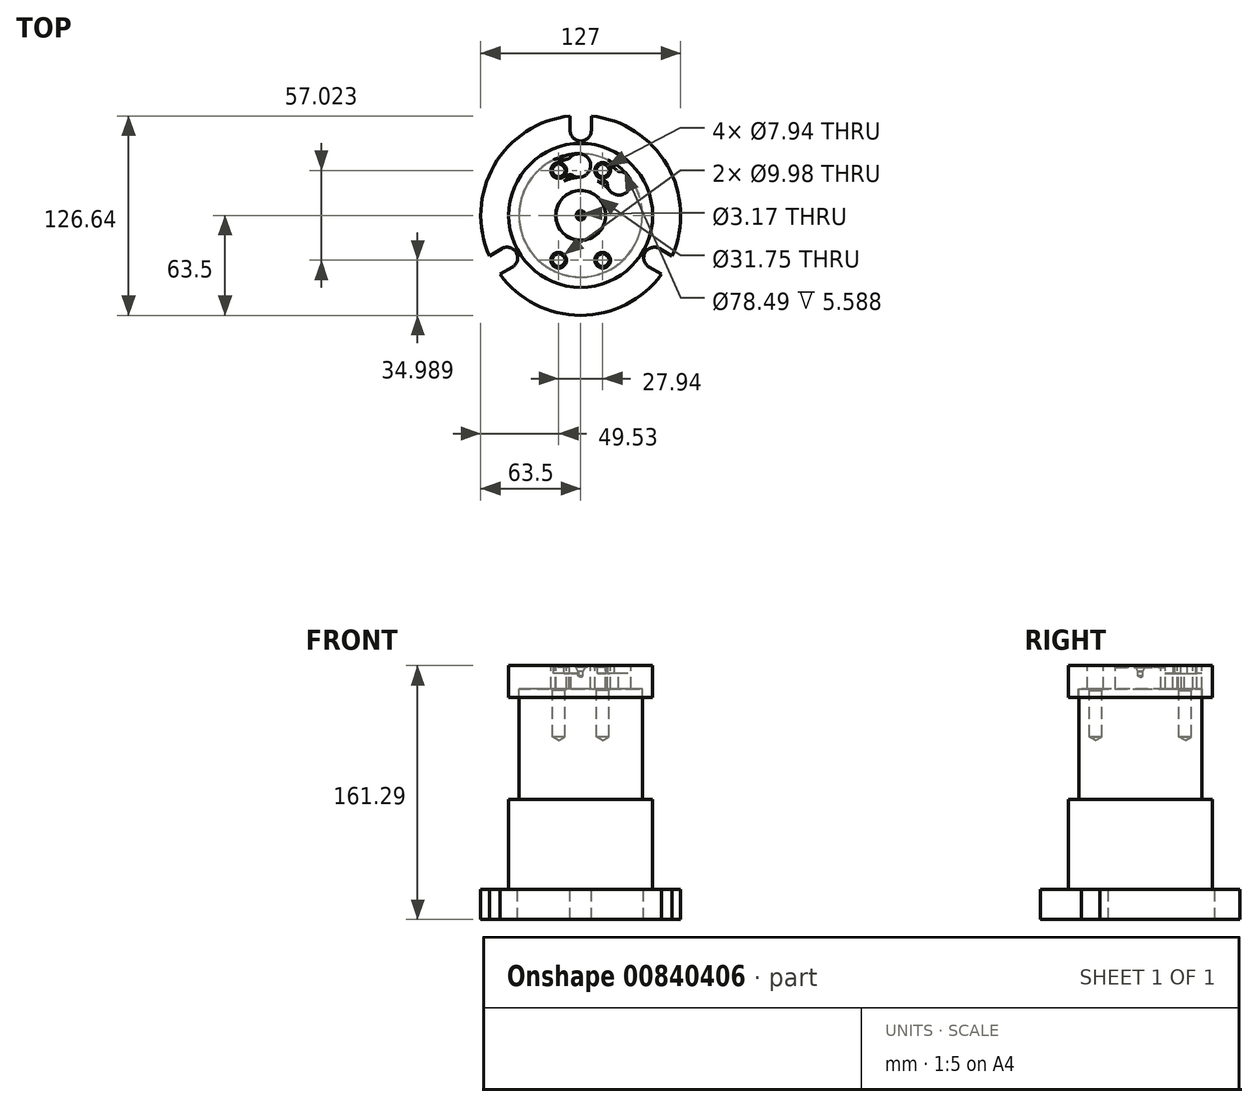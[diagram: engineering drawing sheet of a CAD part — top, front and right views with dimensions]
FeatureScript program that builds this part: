
annotation { "Feature Type Name" : "Feature", "Feature Type Description" : "" }
export const myFeature = defineFeature(function(context is Context, id is Id, definition is map)
    precondition{}
    {
        {
            var Q0;
            Q0=qCreatedBy(makeId("Front.planeOp"),FACE);
            var sketch = newSketch(context, id + "F0", { "sketchPlane" : qUnion([Q0])});
            skLineSegment(sketch, "E0", {"start": v(0, 0) * mm, "end": v(0, -38.57) * mm, "construction": true});
            skLineSegment(sketch, "E1", {"start": v(-15.88, 0) * mm, "end": v(-15.88, -14.73) * mm});
            skLineSegment(sketch, "E2", {"start": v(-15.88, -14.73) * mm, "end": v(-39.24, -14.73) * mm});
            skLineSegment(sketch, "E3", {"start": v(-39.24, -14.73) * mm, "end": v(-39.24, -20.32) * mm});
            skLineSegment(sketch, "E4", {"start": v(-39.24, -20.32) * mm, "end": v(-45.72, -20.32) * mm});
            skLineSegment(sketch, "E5", {"start": v(-45.72, -20.32) * mm, "end": v(-45.72, 0) * mm});
            skLineSegment(sketch, "E6", {"start": v(-45.72, 0) * mm, "end": v(-15.88, 0) * mm});
            skSolve(sketch);
        }
        {
            var Q0;
            Q0 = qSketchRegion(id + "F0", true);
            var Q1;
            Q1=sQuery(id+"F0.wireOp",EDGE,"E0");
            revolve(context, id + "F1", {"surfaceOperationType" : NewSurfaceOperationType.NEW, "entities" : qUnion([Q0]), "axis" : qUnion([Q1]), "revolveType" : RevolveType.FULL});
        }
        {
            var Q0;
            Q0=makeQuery(id+"F1.opRevolve","SWEPT_FACE",FACE,{"disambiguationData":[OSD([sQuery(id+"F0.wireOp",EDGE,"E6")])]});
            var sketch = newSketch(context, id + "F2", { "sketchPlane" : qUnion([Q0])});
            skCircle(sketch, "E7", {"center": v(0, 0) * mm, "radius": 31.75 * mm, "construction": true});
            skCircle(sketch, "E8", {"center": v(-13.97, 28.51) * mm, "radius": 5 * mm});
            skCircle(sketch, "E9", {"center": v(13.97, 28.51) * mm, "radius": 5 * mm});
            skCircle(sketch, "E10", {"center": v(13.97, -28.51) * mm, "radius": 5 * mm});
            skCircle(sketch, "E11", {"center": v(-13.97, -28.51) * mm, "radius": 5 * mm});
            skLineSegment(sketch, "E12", {"start": v(-13.97, 28.51) * mm, "end": v(13.97, 28.51) * mm, "construction": true});
            skLineSegment(sketch, "E13", {"start": v(-13.97, -28.51) * mm, "end": v(13.97, -28.51) * mm, "construction": true});
            skSolve(sketch);
        }
        {
            var Q0;
            Q0 = qSketchRegion(id + "F2", true);
            extrude(context, id + "F3", {"entities" : qUnion([Q0]), "operationType" : NewBodyOperationType.REMOVE, "endBound" : BoundingType.THROUGH_ALL, "oppositeDirection" : true, "depth" : 25.4 * mm, "offsetDistance" : 25.4 * mm});
        }
        {
            var Q0;
            Q0=makeQuery(id+"F1.opRevolve","SWEPT_FACE",FACE,{"disambiguationData":[OSD([sQuery(id+"F0.wireOp",EDGE,"E6")])]});
            var sketch = newSketch(context, id + "F4", { "sketchPlane" : qUnion([Q0])});
            skCircle(sketch, "E14", {"center": v(0, 0) * mm, "radius": 31.75 * mm, "construction": true});
            skPoint(sketch, "E15", {"position": v(-13.97, 28.51) * mm});
            skArc(sketch, "E16", {"start": v(-6.07, 26.06) * mm, "mid": v(6.27, 32.66) * mm, "end": v(-7.32, 36) * mm});
            skLineSegment(sketch, "E17", {"start": v(0, 0) * mm, "end": v(-1.17, 31.73) * mm, "construction": true});
            skLineSegment(sketch, "E18", {"start": v(0, 0) * mm, "end": v(-13.97, 28.51) * mm, "construction": true});
            skArc(sketch, "E19", {"start": v(16.88, 20.77) * mm, "mid": v(29.65, 15.06) * mm, "end": v(23.97, 27.85) * mm});
            skPoint(sketch, "E20", {"position": v(13.97, 28.51) * mm});
            skLineSegment(sketch, "E21", {"start": v(0, 0) * mm, "end": v(13.97, 28.51) * mm, "construction": true});
            skLineSegment(sketch, "E22", {"start": v(0, 0) * mm, "end": v(24.36, 20.36) * mm, "construction": true});
            skArc(sketch, "E23.0", {"start": v(16.17, 33) * mm, "mid": v(9.49, 30.7) * mm, "end": v(11.77, 24.03) * mm});
            skArc(sketch, "E23.1", {"start": v(-16.17, 33) * mm, "mid": v(-18.45, 26.32) * mm, "end": v(-11.77, 24.03) * mm});
            skArc(sketch, "E24", {"start": v(23.97, 27.85) * mm, "mid": v(20.23, 30.67) * mm, "end": v(16.17, 33) * mm});
            skArc(sketch, "E25.trimOffspring", {"start": v(-6.07, 26.06) * mm, "mid": v(-8.98, 25.2) * mm, "end": v(-11.77, 24.03) * mm});
            skArc(sketch, "E26.trimOffspring", {"start": v(-7.32, 36) * mm, "mid": v(-11.84, 34.78) * mm, "end": v(-16.17, 33) * mm});
            skArc(sketch, "E27.trimOffspring", {"start": v(16.88, 20.77) * mm, "mid": v(14.42, 22.54) * mm, "end": v(11.77, 24.03) * mm});
            skSolve(sketch);
        }
        {
            var Q0;
            Q0 = qSketchRegion(id + "F4", true);
            extrude(context, id + "F5", {"entities" : qUnion([Q0]), "operationType" : NewBodyOperationType.REMOVE, "endBound" : BoundingType.THROUGH_ALL, "oppositeDirection" : true, "depth" : 25.4 * mm, "offsetDistance" : 25.4 * mm});
        }
        {
            var Q0;
            Q0=makeQuery(id+"F1.opRevolve","SWEPT_FACE",FACE,{"disambiguationData":[OSD([sQuery(id+"F0.wireOp",EDGE,"E6")])]});
            var sketch = newSketch(context, id + "F6", { "sketchPlane" : qUnion([Q0])});
            skCircle(sketch, "E28", {"center": v(-13.97, 28.51) * mm, "radius": 7.5 * mm});
            skCircle(sketch, "E29", {"center": v(13.97, 28.51) * mm, "radius": 7.5 * mm});
            skCircle(sketch, "E30", {"center": v(0, 0) * mm, "radius": 24.26 * mm});
            skCircle(sketch, "E31", {"center": v(0, 0) * mm, "radius": 39.24 * mm});
            skSolve(sketch);
        }
        {
            var Q0;
            {var subQ0=makeQuery(id+"F5.boolean.opBoolean","COPY",EDGE,{"derivedFrom":makeQuery(id+"F5.opExtrude","CAP_EDGE",EDGE,{"disambiguationData":[OSD([sQuery(id+"F4.wireOp",EDGE,"E25.trimOffspring")])],"isStart":true})});Q0=makeQuery(id+"F6.imprint","IMPRINT",FACE,{"disambiguationData":[TD([[makeQuery(id+"F6.imprint","IMPRINT",EDGE,{"derivedFrom":subQ0}),1.0]])]});}
            var Q1;
            {var subQ0=sQuery(id+"F6.wireOp",EDGE,"E30");var subQ1=sQuery(id+"F6.wireOp",EDGE,"E28");var subQ2=makeQuery(id+"F6.imprint","INTERSECT",VERTEX,{"derivedFrom":[subQ1,subQ0]});Q1=makeQuery(id+"F6.imprint","IMPRINT",FACE,{"disambiguationData":[TD([[makeQuery(id+"F6.imprint","IMPRINT",EDGE,{"disambiguationData":[TD([[subQ2,-1.0]])],"derivedFrom":subQ1}),-1.0]])]});}
            var Q2;
            {var subQ0=sQuery(id+"F6.wireOp",EDGE,"E31");var subQ1=sQuery(id+"F6.wireOp",EDGE,"E28");var subQ2=makeQuery(id+"F6.imprint","INTERSECT",VERTEX,{"derivedFrom":[subQ1,subQ0]});Q2=makeQuery(id+"F6.imprint","IMPRINT",FACE,{"disambiguationData":[TD([[makeQuery(id+"F6.imprint","IMPRINT",EDGE,{"disambiguationData":[TD([[subQ2,1.0]])],"derivedFrom":subQ1}),-1.0]])]});}
            var Q3;
            {var subQ10=makeQuery(id+"F5.boolean.opBoolean","COPY",EDGE,{"derivedFrom":makeQuery(id+"F5.opExtrude","CAP_EDGE",EDGE,{"disambiguationData":[OSD([sQuery(id+"F4.wireOp",EDGE,"E24")])],"isStart":true})});Q3=makeQuery(id+"F6.imprint","IMPRINT",FACE,{"disambiguationData":[TD([[makeQuery(id+"F6.imprint","IMPRINT",EDGE,{"derivedFrom":subQ10}),-1.0]])]});}
            var Q4;
            {var subQ0=sQuery(id+"F6.wireOp",EDGE,"E31");var subQ1=sQuery(id+"F6.wireOp",EDGE,"E29");var subQ2=makeQuery(id+"F6.imprint","INTERSECT",VERTEX,{"derivedFrom":[subQ1,subQ0]});Q4=makeQuery(id+"F6.imprint","IMPRINT",FACE,{"disambiguationData":[TD([[makeQuery(id+"F6.imprint","IMPRINT",EDGE,{"disambiguationData":[TD([[subQ2,1.0]])],"derivedFrom":subQ1}),-1.0]])]});}
            var Q5;
            {var subQ0=sQuery(id+"F6.wireOp",EDGE,"E30");var subQ1=sQuery(id+"F6.wireOp",EDGE,"E29");var subQ2=makeQuery(id+"F6.imprint","INTERSECT",VERTEX,{"derivedFrom":[subQ1,subQ0]});Q5=makeQuery(id+"F6.imprint","IMPRINT",FACE,{"disambiguationData":[TD([[makeQuery(id+"F6.imprint","IMPRINT",EDGE,{"disambiguationData":[TD([[subQ2,-1.0]])],"derivedFrom":subQ1}),-1.0]])]});}
            var Q6;
            {var subQ0=makeQuery(id+"F3.boolean.opBoolean","COPY",EDGE,{"derivedFrom":makeQuery(id+"F3.opExtrude","CAP_EDGE",EDGE,{"disambiguationData":[OSD([sQuery(id+"F2.wireOp",EDGE,"E8")])],"isStart":true})});Q6=makeQuery(id+"F6.imprint","IMPRINT",FACE,{"disambiguationData":[TD([[makeQuery(id+"F6.imprint","IMPRINT",EDGE,{"derivedFrom":subQ0}),-1.0]])]});}
            var Q7;
            {var subQ4=makeQuery(id+"F3.boolean.opBoolean","COPY",EDGE,{"derivedFrom":makeQuery(id+"F3.opExtrude","CAP_EDGE",EDGE,{"disambiguationData":[OSD([sQuery(id+"F2.wireOp",EDGE,"E9")])],"isStart":true})});Q7=makeQuery(id+"F6.imprint","IMPRINT",FACE,{"disambiguationData":[TD([[makeQuery(id+"F6.imprint","IMPRINT",EDGE,{"derivedFrom":subQ4}),-1.0]])]});}
            extrude(context, id + "F7", {"entities" : qUnion([Q0, Q1, Q2, Q3, Q4, Q5, Q6, Q7]), "operationType" : NewBodyOperationType.REMOVE, "oppositeDirection" : true, "depth" : 5.08 * mm, "offsetDistance" : 25.4 * mm});
        }
        {
            var Q0;
            Q0=qCreatedBy(makeId("Right.planeOp"),FACE);
            var sketch = newSketch(context, id + "F8", { "sketchPlane" : qUnion([Q0])});
            skLineSegment(sketch, "E32", {"start": v(-39.12, -85.1) * mm, "end": v(-39.12, -14.73) * mm});
            skLineSegment(sketch, "E33", {"start": v(-39.12, -14.73) * mm, "end": v(-15.75, -14.73) * mm});
            skLineSegment(sketch, "E34", {"start": v(-15.75, -14.73) * mm, "end": v(-15.75, -1.27) * mm});
            skLineSegment(sketch, "E35", {"start": v(-15.75, -1.27) * mm, "end": v(0, -1.27) * mm});
            skLineSegment(sketch, "E36", {"start": v(0, -1.27) * mm, "end": v(0, -161.3) * mm});
            skLineSegment(sketch, "E37", {"start": v(0, -161.3) * mm, "end": v(-63.5, -161.3) * mm});
            skLineSegment(sketch, "E38", {"start": v(-63.5, -161.3) * mm, "end": v(-63.5, -142.24) * mm});
            skLineSegment(sketch, "E39", {"start": v(-63.5, -142.24) * mm, "end": v(-45.72, -142.24) * mm});
            skLineSegment(sketch, "E40", {"start": v(-45.72, -142.24) * mm, "end": v(-45.72, -85.1) * mm});
            skLineSegment(sketch, "E41", {"start": v(-45.72, -85.1) * mm, "end": v(-39.12, -85.1) * mm});
            skLineSegment(sketch, "E42", {"start": v(0, 32.69) * mm, "end": v(0, -171.35) * mm, "construction": true});
            skSolve(sketch);
        }
        {
            var Q0;
            Q0 = qSketchRegion(id + "F8", true);
            var Q1;
            Q1=sQuery(id+"F8.wireOp",EDGE,"E42");
            revolve(context, id + "F9", {"surfaceOperationType" : NewSurfaceOperationType.NEW, "entities" : qUnion([Q0]), "axis" : qUnion([Q1]), "revolveType" : RevolveType.FULL});
        }
        {
            var Q0;
            Q0=makeQuery(id+"F9.opRevolve","SWEPT_FACE",FACE,{"disambiguationData":[OSD([sQuery(id+"F8.wireOp",EDGE,"E33")])]});
            var sketch = newSketch(context, id + "F10", { "sketchPlane" : qUnion([Q0])});
            skSolve(sketch);
        }
        {
            var Q0;
            {var subQ0=sQuery(id+"F8.wireOp",EDGE,"E33");Q0=makeQuery(id+"F10.imprint","IMPRINT",FACE,{"disambiguationData":[TD([[makeQuery(id+"F10.imprint","IMPRINT",EDGE,{"derivedFrom":makeQuery(id+"F9.opRevolve","SWEPT_EDGE",EDGE,{"disambiguationData":[OSD([sQuery(id+"F8.wireOp",EDGE,"E32"),subQ0])]})}),1.0]])]});}
            var sketch = newSketch(context, id + "F11", { "sketchPlane" : qUnion([Q0])});
            skPoint(sketch, "E43", {"position": v(-13.97, 28.51) * mm});
            skPoint(sketch, "E44", {"position": v(13.97, 28.51) * mm});
            skPoint(sketch, "E45", {"position": v(13.97, -28.51) * mm});
            skPoint(sketch, "E46", {"position": v(-13.97, -28.51) * mm});
            skSolve(sketch);
        }
        {
            var Q0;
            Q0=sQuery(id+"F11.wireOp",VERTEX,"E43");
            var Q1;
            Q1=sQuery(id+"F11.wireOp",VERTEX,"E46");
            var Q2;
            Q2=sQuery(id+"F11.wireOp",VERTEX,"E45");
            var Q3;
            Q3=sQuery(id+"F11.wireOp",VERTEX,"E44");
            var Q4;
            Q4=makeQuery(id+"F9.opRevolve","SWEPT_BODY",BODY,{"disambiguationData":[OSD([sQuery(id+"F8.wireOp",EDGE,"E32"),sQuery(id+"F8.wireOp",EDGE,"E33"),sQuery(id+"F8.wireOp",EDGE,"E34"),sQuery(id+"F8.wireOp",EDGE,"E35"),sQuery(id+"F8.wireOp",EDGE,"E36"),sQuery(id+"F8.wireOp",EDGE,"E37"),sQuery(id+"F8.wireOp",EDGE,"E38"),sQuery(id+"F8.wireOp",EDGE,"E39"),sQuery(id+"F8.wireOp",EDGE,"E40"),sQuery(id+"F8.wireOp",EDGE,"E41")])]});
            hole(context, id + "F12", {"style" : HoleStyle.C_SINK, "endStyle" : HoleEndStyle.BLIND, "holeDiameter" : 7.94 * mm, "cSinkDiameter" : 9.9 * mm, "cSinkAngle" : 90 * degree, "majorDiameter" : 6.35 * mm, "holeDepth" : 30.48 * mm, "isTappedThrough" : true, "tappedDepth" : 12.7 * mm, "tapClearance" : 3, "startFromSketch" : true, "locations" : qUnion([Q0, Q1, Q2, Q3]), "scope" : qUnion([Q4])});
        }
        {
            var Q0;
            Q0=makeQuery(id+"F9.opRevolve","SWEPT_FACE",FACE,{"disambiguationData":[OSD([sQuery(id+"F8.wireOp",EDGE,"E39")])]});
            var sketch = newSketch(context, id + "F13", { "sketchPlane" : qUnion([Q0])});
            skLineSegment(sketch, "E47", {"start": v(0, 53.98) * mm, "end": v(0, 0) * mm, "construction": true});
            skLineSegment(sketch, "E48", {"start": v(0, 0) * mm, "end": v(46.74, -26.99) * mm, "construction": true});
            skLineSegment(sketch, "E49", {"start": v(0, 0) * mm, "end": v(-46.74, -26.99) * mm, "construction": true});
            skArc(sketch, "E50", {"start": v(-6.73, 53.98) * mm, "mid": v(0, 47.24) * mm, "end": v(6.73, 53.98) * mm});
            skArc(sketch, "E51", {"start": v(50.1, -21.16) * mm, "mid": v(40.91, -23.62) * mm, "end": v(43.38, -32.82) * mm});
            skArc(sketch, "E52", {"start": v(-43.38, -32.82) * mm, "mid": v(-40.91, -23.62) * mm, "end": v(-50.1, -21.16) * mm});
            skLineSegment(sketch, "E53", {"start": v(6.73, 53.98) * mm, "end": v(6.73, 67.54) * mm});
            skLineSegment(sketch, "E54", {"start": v(6.73, 67.54) * mm, "end": v(-6.73, 67.54) * mm});
            skLineSegment(sketch, "E55", {"start": v(-6.73, 67.54) * mm, "end": v(-6.73, 53.98) * mm});
            skLineSegment(sketch, "E56", {"start": v(-43.38, -32.82) * mm, "end": v(-66.46, -46.14) * mm});
            skLineSegment(sketch, "E57", {"start": v(-66.46, -46.14) * mm, "end": v(-73.19, -34.48) * mm});
            skLineSegment(sketch, "E58", {"start": v(-73.19, -34.48) * mm, "end": v(-50.1, -21.16) * mm});
            skLineSegment(sketch, "E59", {"start": v(50.1, -21.16) * mm, "end": v(67.54, -31.22) * mm});
            skLineSegment(sketch, "E60", {"start": v(67.54, -31.22) * mm, "end": v(60.81, -42.88) * mm});
            skLineSegment(sketch, "E61", {"start": v(60.81, -42.88) * mm, "end": v(43.38, -32.82) * mm});
            skSolve(sketch);
        }
        {
            var Q0;
            Q0 = qSketchRegion(id + "F13", true);
            extrude(context, id + "F14", {"entities" : qUnion([Q0]), "operationType" : NewBodyOperationType.REMOVE, "oppositeDirection" : true, "depth" : 25.4 * mm, "offsetDistance" : 25.4 * mm});
        }
        {
            var Q0;
            Q0=qCreatedBy(makeId("Right.planeOp"),FACE);
            var sketch = newSketch(context, id + "F15", { "sketchPlane" : qUnion([Q0])});
            skLineSegment(sketch, "E62", {"start": v(2.94, -1.27) * mm, "end": v(1.59, -3.62) * mm});
            skLineSegment(sketch, "E63", {"start": v(1.59, -3.62) * mm, "end": v(1.59, -6.5) * mm});
            skLineSegment(sketch, "E64", {"start": v(1.59, -6.5) * mm, "end": v(0, -7.38) * mm});
            skLineSegment(sketch, "E65", {"start": v(0, -7.38) * mm, "end": v(0, -1.27) * mm});
            skLineSegment(sketch, "E66", {"start": v(0, -1.27) * mm, "end": v(2.94, -1.27) * mm});
            skSolve(sketch);
        }
        {
            var Q0;
            Q0 = qSketchRegion(id + "F15", true);
            var Q1;
            Q1=sQuery(id+"F15.wireOp",EDGE,"E65");
            revolve(context, id + "F16", {"operationType" : NewBodyOperationType.REMOVE, "surfaceOperationType" : NewSurfaceOperationType.NEW, "entities" : qUnion([Q0]), "axis" : qUnion([Q1]), "revolveType" : RevolveType.FULL, "oppositeDirection" : true});
        }
    });
